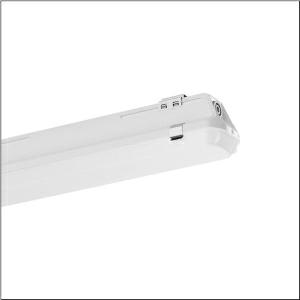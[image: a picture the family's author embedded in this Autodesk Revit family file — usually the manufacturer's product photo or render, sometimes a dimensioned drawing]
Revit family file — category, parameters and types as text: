
# Revit family: monsun_r__21_51fb207p480b_726c
name_source: partatom
category: Lighting Fixtures
units: mm (PartAtom-declared; Revit-internal decimal feet)

## family parameters
Cut with Voids When Loaded = No
Host = Face
Light Source = No
Part Type = Normal
Room Calculation Point = No
Round Connector Dimension = Use Diameter
Shared = No

## types (1)
- Monsun® 21 (1 x LED, 7270 lm, 52.8 W, 4000K)
    Apparent Load = 53 VA
    CIE Flux Codes = 45 75 93 94 100
    Color Rendering = 80
    Color Temperature = 4000K
    Default Elevation = 1800 mm
    Description = Monsun® 21, damp-proof luminaire, chain hanger, primary optical cover: enclosure, of PC, light emission: direct distribution, primary light characteristic: symmetric, installation type: suspended mounting, surface-mounted, horizontal mounting, vertical mounting, LED, rated luminous flux: 7.270lm, luminous efficacy: 138lm/W, light colour: 840, colour temperature: 4000K, control gear: ECG, with terminal, 3-pole, max. 2.5mm², mains connection: 220..240V, AC, 50/60Hz, rated input power: 53W, housing, of glass-fibre reinforced polyester, uncoated, bright grey, incl. chain hanger, length: 1.590mm, width: 90mm, height: 88mm, clip for enclosure, of stainless steel (V2A), ceiling mounting element, of stainless steel (V2A), chain hanger, of stainless steel (V2A), protection rating (complete): IP66, insulation class (complete): insulation class I (protective earthing), certification: CE, ENEC, VDE, UKCA, protection symbol: D, impact resistance: IK08, permissible operating ambient temperature: -25..+35°C, standard: EN 50419, EN 60598-2-1, corresponds to IFS (International Featured Standards) requirements for safety and quality in the food industry, for indoor or canopied outdoor use, no direct snow, no direct sun, no direct rain, contact your sales advisor before using the luminaires in applications with unclear chemical exposure, large temperature fluctuations or condensation-forming humidity, LABS conformity tested according to VDMA 24364:2018-05, packaging unit: 1 piece
    Height = 89 mm
    Lamp = 1 x LED
    Lamp Light Flux = 7270 lm
    Lamp Power = 52.8 W
    Lamp count = 1
    Length = 1590 mm
    Luminous efficacy = 138 lm/W
    Manufacturer = Siteco
    ModVariant = No
    Model = 51FB207P480B
    Mounting Place = Ceiling
    Mounting Type = Surface mounted
    Number of Poles = 1
    OnlyDefault = Yes
    Power Factor = 1
    Product Name = Monsun® 21
    Product group = damp-proof luminaire
    ProductGroupID = 300
    Protection Class = Protection class I
    Protection Degree = IP 66
    RLX_Detail_Level = 1
    RLX_Emergency_Light_Flux = 0 lm
    RLX_Emergency_Type = 0
    RLX_Emergency_Type_DB = No
    RlxData = <blob elided: 88665 chars, md5=1459f8ed>
    Socket = socket
    Standby Power = 0 W
    System Light Flux = 7270 lm
    System Power = 53 W
    Type Comments = Product without accessories
    Type Image = l_1006717.jpg
    URL = http://relux.com
    VarID = ---
    Voltage = 0 V
    Weight = 0.00 kg
    Width = 90 mm

## geometry (parser evidence)
native form markers: Blend x4, Sweep x13
no freeform markers — native parametric forms only
